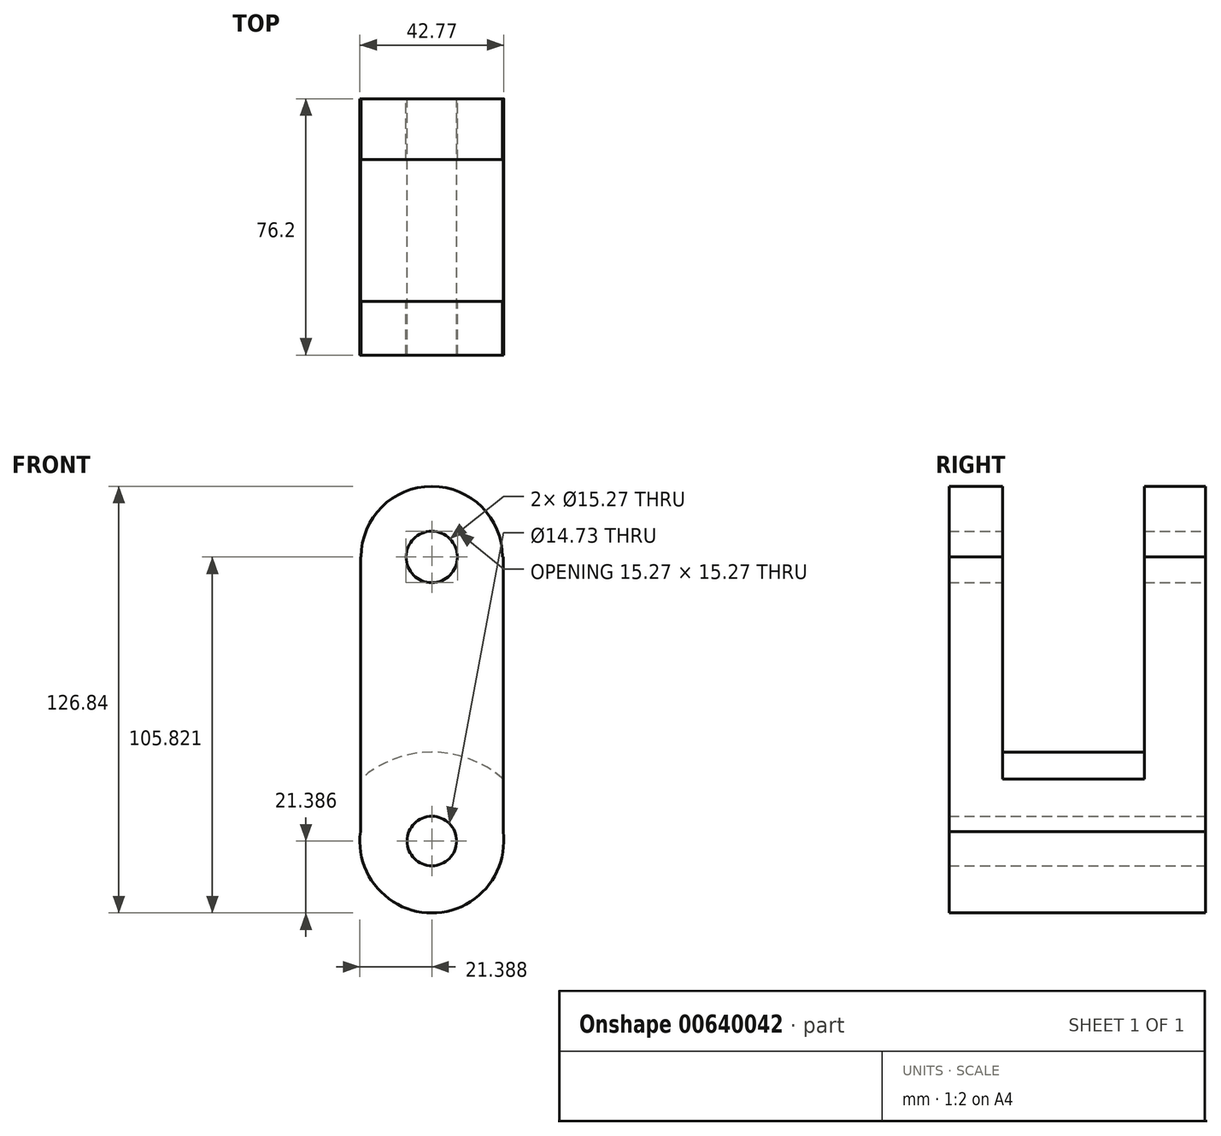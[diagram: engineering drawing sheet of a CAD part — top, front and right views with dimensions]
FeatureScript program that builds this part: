
annotation { "Feature Type Name" : "Feature", "Feature Type Description" : "" }
export const myFeature = defineFeature(function(context is Context, id is Id, definition is map)
    precondition{}
    {
        {
            var Q0;
            Q0=qCreatedBy(makeId("Front.planeOp"),FACE);
            var sketch = newSketch(context, id + "F0", { "sketchPlane" : qUnion([Q0])});
            skLineSegment(sketch, "E0.bottom", {"start": v(-24.24, 46.18) * mm, "end": v(18.16, 46.18) * mm});
            skLineSegment(sketch, "E0.top", {"start": v(-24.24, -38.25) * mm, "end": v(18.16, -38.25) * mm});
            skLineSegment(sketch, "E0.left", {"start": v(-24.24, 46.18) * mm, "end": v(-24.24, -38.25) * mm});
            skLineSegment(sketch, "E0.right", {"start": v(18.16, 46.18) * mm, "end": v(18.16, -38.25) * mm});
            skCircle(sketch, "E1", {"center": v(-3.04, 46.18) * mm, "radius": 21.01 * mm});
            skCircle(sketch, "E2", {"center": v(-3.04, -38.25) * mm, "radius": 21.39 * mm});
            skCircle(sketch, "E3", {"center": v(-3.04, 46.18) * mm, "radius": 7.64 * mm});
            skCircle(sketch, "E4", {"center": v(-3.04, -38.25) * mm, "radius": 7.36 * mm});
            skSolve(sketch);
        }
        {
            var Q0;
            {var subQ0=sQuery(id+"F0.wireOp",EDGE,"E1");var subQ1=sQuery(id+"F0.wireOp",EDGE,"E0.bottom");var subQ2=makeQuery(id+"F0.imprint","INTERSECT",VERTEX,{"disambiguationData":[OD(0.0)],"derivedFrom":[subQ1,subQ0]});Q0=makeQuery(id+"F0.imprint","IMPRINT",FACE,{"disambiguationData":[TD([[makeQuery(id+"F0.imprint","IMPRINT",EDGE,{"disambiguationData":[TD([[subQ2,-1.0]])],"derivedFrom":subQ1}),1.0]])]});}
            var Q1;
            {var subQ0=sQuery(id+"F0.wireOp",EDGE,"E1");var subQ1=sQuery(id+"F0.wireOp",EDGE,"E0.bottom");var subQ2=makeQuery(id+"F0.imprint","INTERSECT",VERTEX,{"disambiguationData":[OD(0.0)],"derivedFrom":[subQ1,subQ0]});Q1=makeQuery(id+"F0.imprint","IMPRINT",FACE,{"disambiguationData":[TD([[makeQuery(id+"F0.imprint","IMPRINT",EDGE,{"disambiguationData":[TD([[subQ2,-1.0]])],"derivedFrom":subQ1}),-1.0]])]});}
            var Q2;
            {var subQ0=sQuery(id+"F0.wireOp",EDGE,"E0.left");var subQ1=sQuery(id+"F0.wireOp",EDGE,"E0.bottom");var subQ2=makeQuery(id+"F0.imprint","INTERSECT",VERTEX,{"derivedFrom":[subQ1,subQ0]});Q2=makeQuery(id+"F0.imprint","IMPRINT",FACE,{"disambiguationData":[TD([[makeQuery(id+"F0.imprint","IMPRINT",EDGE,{"disambiguationData":[TD([[subQ2,-1.0]])],"derivedFrom":subQ1}),-1.0]])]});}
            var Q3;
            {var subQ1=sQuery(id+"F0.wireOp",EDGE,"E0.top");var subQ5=sQuery(id+"F0.wireOp",EDGE,"E0.left");var subQ6=makeQuery(id+"F0.imprint","INTERSECT",VERTEX,{"derivedFrom":[subQ1,subQ5]});Q3=makeQuery(id+"F0.imprint","IMPRINT",FACE,{"disambiguationData":[TD([[makeQuery(id+"F0.imprint","IMPRINT",EDGE,{"disambiguationData":[TD([[subQ6,-1.0]])],"derivedFrom":subQ1}),1.0]])]});}
            var Q4;
            {var subQ1=sQuery(id+"F0.wireOp",EDGE,"E0.top");var subQ5=sQuery(id+"F0.wireOp",EDGE,"E0.left");var subQ6=makeQuery(id+"F0.imprint","INTERSECT",VERTEX,{"derivedFrom":[subQ1,subQ5]});Q4=makeQuery(id+"F0.imprint","IMPRINT",FACE,{"disambiguationData":[TD([[makeQuery(id+"F0.imprint","IMPRINT",EDGE,{"disambiguationData":[TD([[subQ6,-1.0]])],"derivedFrom":subQ1}),-1.0]])]});}
            extrude(context, id + "F1", {"entities" : qUnion([Q0, Q1, Q2, Q3, Q4]), "depth" : 76.2 * mm, "offsetDistance" : 25.4 * mm});
        }
        {
            var Q0;
            Q0=makeQuery(id+"F1.opExtrude","SWEPT_FACE",FACE,{"disambiguationData":[OSD([sQuery(id+"F0.wireOp",EDGE,"E0.right")])]});
            var sketch = newSketch(context, id + "F2", { "sketchPlane" : qUnion([Q0])});
            skLineSegment(sketch, "E5.bottom", {"start": v(-60.23, -19.87) * mm, "end": v(-18.12, -19.87) * mm});
            skLineSegment(sketch, "E5.top", {"start": v(-60.23, 72.7) * mm, "end": v(-18.12, 72.7) * mm});
            skLineSegment(sketch, "E5.left", {"start": v(-60.23, -19.87) * mm, "end": v(-60.23, 72.7) * mm});
            skLineSegment(sketch, "E5.right", {"start": v(-18.12, -19.87) * mm, "end": v(-18.12, 72.7) * mm});
            skSolve(sketch);
        }
        {
            var Q0;
            {var subQ0=sQuery(id+"F2.wireOp",EDGE,"E5.top");Q0=makeQuery(id+"F2.imprint","IMPRINT",FACE,{"disambiguationData":[TD([[makeQuery(id+"F2.imprint","IMPRINT",EDGE,{"derivedFrom":subQ0}),-1.0]])]});}
            var Q1;
            {var subQ0=sQuery(id+"F2.wireOp",EDGE,"E5.bottom");Q1=makeQuery(id+"F2.imprint","IMPRINT",FACE,{"disambiguationData":[TD([[makeQuery(id+"F2.imprint","IMPRINT",EDGE,{"derivedFrom":subQ0}),1.0]])]});}
            extrude(context, id + "F3", {"entities" : qUnion([Q0, Q1]), "operationType" : NewBodyOperationType.REMOVE, "oppositeDirection" : true, "depth" : 127 * mm, "offsetDistance" : 25.4 * mm});
        }
        {
            var Q0;
            Q0=makeQuery(id+"F3.boolean.opBoolean","COPY",FACE,{"derivedFrom":makeQuery(id+"F3.opExtrude","SWEPT_FACE",FACE,{"disambiguationData":[OSD([sQuery(id+"F2.wireOp",EDGE,"E5.right")])]})});
            var sketch = newSketch(context, id + "F4", { "sketchPlane" : qUnion([Q0])});
            skArc(sketch, "E6", {"start": v(18.16, -19.87) * mm, "mid": v(-3.04, -11.82) * mm, "end": v(-24.24, -19.87) * mm});
            skSolve(sketch);
        }
        {
            var Q0;
            Q0=makeQuery(id+"F4.imprint","IMPRINT",FACE,{"disambiguationData":[TD([[makeQuery(id+"F4.imprint","IMPRINT",EDGE,{"derivedFrom":sQuery(id+"F4.wireOp",EDGE,"E6")}),1.0]])]});
            extrude(context, id + "F5", {"entities" : qUnion([Q0]), "operationType" : NewBodyOperationType.ADD, "depth" : 45.72 * mm, "offsetDistance" : 25.4 * mm});
        }
    });
